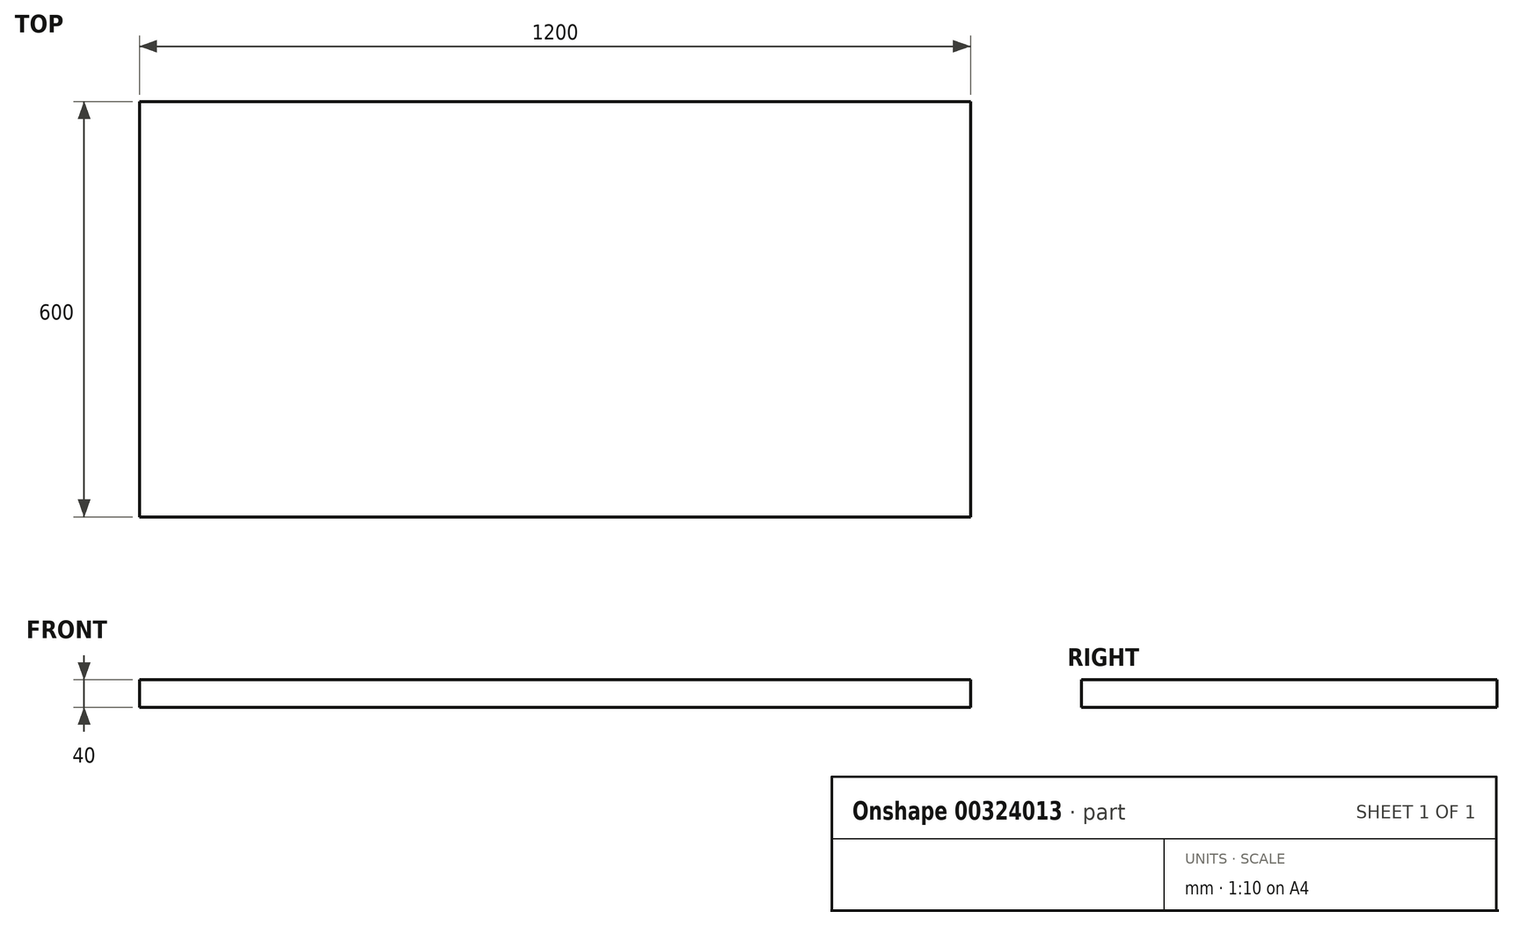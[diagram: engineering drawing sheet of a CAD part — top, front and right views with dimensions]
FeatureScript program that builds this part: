
annotation { "Feature Type Name" : "Feature", "Feature Type Description" : "" }
export const myFeature = defineFeature(function(context is Context, id is Id, definition is map)
    precondition{}
    {
        {
            var Q0;
            Q0=qCreatedBy(makeId("Top.planeOp"),FACE);
            var sketch = newSketch(context, id + "F0", { "sketchPlane" : qUnion([Q0])});
            skLineSegment(sketch, "E0.bottom", {"start": v(-600, 300) * mm, "end": v(600, 300) * mm});
            skLineSegment(sketch, "E0.top", {"start": v(-600, -300) * mm, "end": v(600, -300) * mm});
            skLineSegment(sketch, "E0.left", {"start": v(-600, 300) * mm, "end": v(-600, -300) * mm});
            skLineSegment(sketch, "E0.right", {"start": v(600, 300) * mm, "end": v(600, -300) * mm});
            skPoint(sketch, "E0.middle", {"position": v(0, 0) * mm});
            skSolve(sketch);
        }
        {
            var Q0;
            Q0=makeQuery(id+"F0.imprint","IMPRINT",FACE,{"disambiguationData":[TD([[makeQuery(id+"F0.imprint","IMPRINT",EDGE,{"derivedFrom":sQuery(id+"F0.wireOp",EDGE,"E0.bottom")}),-1.0]])]});
            extrude(context, id + "F1", {"entities" : qUnion([Q0]), "depth" : 40 * mm});
        }
    });
